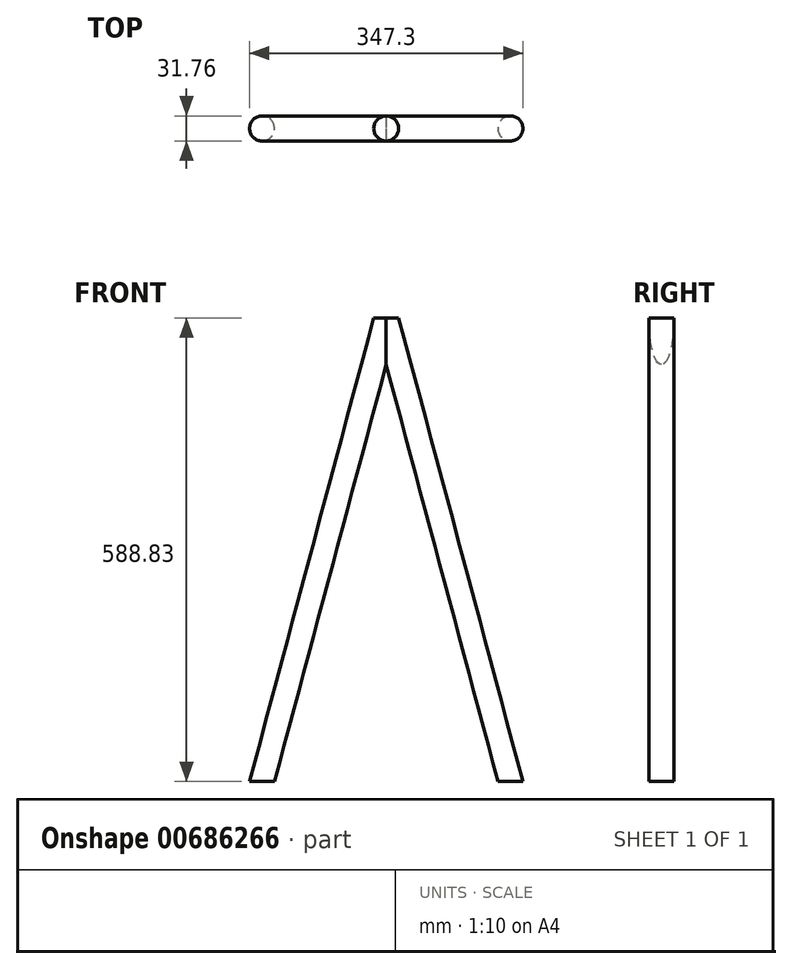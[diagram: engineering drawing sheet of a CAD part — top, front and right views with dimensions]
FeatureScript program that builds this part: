
annotation { "Feature Type Name" : "Feature", "Feature Type Description" : "" }
export const myFeature = defineFeature(function(context is Context, id is Id, definition is map)
    precondition{}
    {
        {
            var Q0;
            Q0=qCreatedBy(makeId("Front.planeOp"),FACE);
            var sketch = newSketch(context, id + "F0", { "sketchPlane" : qUnion([Q0])});
            skLineSegment(sketch, "E0", {"start": v(0, 588.83) * mm, "end": v(-157.78, 0) * mm});
            skLineSegment(sketch, "E1", {"start": v(0, 588.83) * mm, "end": v(157.78, 0) * mm});
            skSolve(sketch);
        }
        {
            var Q0;
            Q0=qCreatedBy(makeId("Top.planeOp"),FACE);
            var sketch = newSketch(context, id + "F1", { "sketchPlane" : qUnion([Q0])});
            skCircle(sketch, "E2", {"center": v(-157.78, 0) * mm, "radius": 15.87 * mm});
            skCircle(sketch, "E3", {"center": v(157.78, 0) * mm, "radius": 15.88 * mm});
            skSolve(sketch);
        }
        {
            var Q0;
            Q0=makeQuery(id+"F1.imprint","IMPRINT",FACE,{"disambiguationData":[TD([[makeQuery(id+"F1.imprint","IMPRINT",EDGE,{"derivedFrom":sQuery(id+"F1.wireOp",EDGE,"E3")}),1.0]])]});
            var Q1;
            Q1=sQuery(id+"F0.wireOp",EDGE,"E1");
            sweep(context, id + "F2", {"profiles" : qUnion([Q0]), "path" : qUnion([Q1])});
        }
        {
            var Q0;
            Q0=makeQuery(id+"F1.imprint","IMPRINT",FACE,{"disambiguationData":[TD([[makeQuery(id+"F1.imprint","IMPRINT",EDGE,{"derivedFrom":sQuery(id+"F1.wireOp",EDGE,"E2")}),1.0]])]});
            var Q1;
            Q1=sQuery(id+"F0.wireOp",EDGE,"E0");
            sweep(context, id + "F3", {"operationType" : NewBodyOperationType.ADD, "profiles" : qUnion([Q0]), "path" : qUnion([Q1])});
        }
    });
